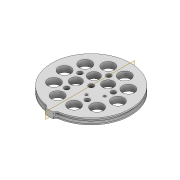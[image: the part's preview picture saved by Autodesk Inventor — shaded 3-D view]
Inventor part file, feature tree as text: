
AUTODESK INVENTOR PART (.ipt)
format: ipt  version: 2022 (Build 260153000, 153)  size: 404,480 bytes
history: native  units: mm
features: extrude x8, sketch x7, plane x3, fillet x2, projected_geometry x2, pattern_circular x1, mirror x1
ambient origin geometry x8: Origin, YZ Plane, XZ Plane, XY Plane, X Axis, Y Axis, Z Axis, Center Point
bodies: Solid1 (feature_tree)
feature tree (24):
  extrude  "Extrusion1"  Depth=60.0mm
  extrude  "Extrusion2"  Depth=3.0mm TaperAngle=0.0deg
  pattern_circular  "Circular Pattern1"  Count=5 Angle=360.0deg
  plane  "Work Plane1"
  plane  "Work Plane2"
  extrude  "Extrusion3"  [1 undecoded]
  extrude  "Extrusion4"  Depth=3.0mm
  fillet  "Fillet1"  Radius=1.7mm
  plane  "Work Plane3"
  extrude  "Extrusion9"  Depth=10.0mm TaperAngle=0.0deg
  mirror  "Mirror1"
  sketch  "Sketch9"  dims[d13=9.599311mm d14=-9.599311mm]
  extrude  "Extrusion10"  Depth=3.0mm
  extrude  "Extrusion11"  Depth=3.0mm
  extrude  "Extrusion12"  Depth=3.0mm
  fillet  "Fillet3"  Radius=10.0mm
  sketch  "Sketch1"  dims[d0=4.2mm d2=60.0mm]
  sketch  "Sketch2"  dims[d3=4.0mm d4=3.0mm d5=0.0mm]
  sketch  "Sketch3"  dims[d6=9.0mm]
  sketch  "Sketch4"  dims[d7=10.0mm]
  sketch  "Sketch8"  dims[d8=10.0mm d9=0.0mm d10=50.0mm d11=360.0deg]
  projected_geometry  "Projected Loop3"
  projected_geometry  "Projected Loop4"
  sketch  "Sketch10"  dims[d15=1.5mm d16=1.5mm d17=1.7mm d18=10.0mm d19=0.0mm d20=1.5mm d21=1.5mm d22=1.7mm d23=10.0mm d24=0.0mm d25=1.0mm d46=22.0mm d47=3.141593mm d48=22.0mm d49=10.0mm d50=10.0mm d51=4.0mm d52=14.5mm d53=6.283185mm d54=4.0mm d55=14.5mm d56=65.0mm d57=1.0mm d58=0.0mm d59=2.1mm d60=2.1mm d61=4.5mm d62=8.4mm d63=1.9mm d64=13.0mm d65=5.0mm d66=0.0mm d67=100.0mm d68=0.0mm d69=2.0mm d70=2.0mm d72=3.0mm d73=5.0mm d74=0.0mm d75=3.0mm]
note: 1 required parameter value undecoded (feature->parameter linkage not recoverable at this tier; creation-order binding heuristic only, values carry confidence <= 0.55)
